FCSTD DOCUMENT  (FreeCAD 0.20R29603 (Git))
Label: samd21pad
License: All rights reserved
LicenseURL: http://en.wikipedia.org/wiki/All_rights_reserved
objects: Sketcher::SketchObject×1
note: 1 computed .brp shape members not serialized (recipe doc carries the construction recipe); baked Part::Feature solids carry a one-line shape summary decoded from their .brp

FEATURE [Sketcher::SketchObject] Sketch  label="Edge Cuts"
  FullyConstrained = false
  sketch-geometry (63):
    g0: ArcOfCircle CenterX=-27.575 CenterY=27.575 CenterZ=0 NormalX=0 NormalY=0 NormalZ=1 AngleXU=0 Radius=1 StartAngle=1.5708 EndAngle=3.14159
    g1: LineSegment StartX=-27.575 StartY=28.575 StartZ=0 EndX=27.575 EndY=28.575 EndZ=0
    g2: ArcOfCircle CenterX=27.575 CenterY=27.575 CenterZ=0 NormalX=0 NormalY=0 NormalZ=1 AngleXU=0 Radius=1 StartAngle=-9e-16 EndAngle=1.5708
    g3: ArcOfCircle CenterX=27.575 CenterY=-27.575 CenterZ=0 NormalX=0 NormalY=0 NormalZ=1 AngleXU=0 Radius=1 StartAngle=4.71239 EndAngle=6.28319
    g4: LineSegment StartX=27.575 StartY=-28.575 StartZ=0 EndX=-27.575 EndY=-28.575 EndZ=0
    g5: ArcOfCircle CenterX=-27.575 CenterY=-27.575 CenterZ=0 NormalX=0 NormalY=0 NormalZ=1 AngleXU=0 Radius=1 StartAngle=3.14159 EndAngle=4.71239
    g6: LineSegment StartX=-28.575 StartY=-27.575 StartZ=0 EndX=-28.575 EndY=27.575 EndZ=0
    g7: GeomPoint X=-28.575 Y=28.575 Z=0
    g8: GeomPoint X=28.575 Y=-28.575 Z=0
    g9: ArcOfCircle CenterX=34.575 CenterY=27.575 CenterZ=0 NormalX=0 NormalY=0 NormalZ=1 AngleXU=0 Radius=1 StartAngle=1.5708 EndAngle=3.14159
    g10: LineSegment StartX=34.575 StartY=28.575 StartZ=0 EndX=89.725 EndY=28.575 EndZ=0
    g11: ArcOfCircle CenterX=89.725 CenterY=27.575 CenterZ=0 NormalX=0 NormalY=0 NormalZ=1 AngleXU=0 Radius=1 StartAngle=-9e-16 EndAngle=1.5708
    g12: LineSegment StartX=90.725 StartY=27.575 StartZ=0 EndX=90.725 EndY=-27.575 EndZ=0
    g13: ArcOfCircle CenterX=89.725 CenterY=-27.575 CenterZ=0 NormalX=0 NormalY=0 NormalZ=1 AngleXU=0 Radius=1 StartAngle=4.71239 EndAngle=6.28319
    g14: ArcOfCircle CenterX=34.575 CenterY=-27.575 CenterZ=0 NormalX=0 NormalY=0 NormalZ=1 AngleXU=0 Radius=1 StartAngle=3.14159 EndAngle=4.71239
    g15: GeomPoint X=37.8345 Y=28.575 Z=0
    g16: GeomPoint X=90.725 Y=-28.575 Z=0
    g17: ArcOfCircle CenterX=34.575 CenterY=-34.575 CenterZ=0 NormalX=0 NormalY=0 NormalZ=1 AngleXU=0 Radius=1 StartAngle=1.5708 EndAngle=3.14159
    g18: ArcOfCircle CenterX=89.725 CenterY=-34.575 CenterZ=0 NormalX=0 NormalY=0 NormalZ=1 AngleXU=0 Radius=1 StartAngle=-9e-16 EndAngle=1.5708
    g19: LineSegment StartX=90.725 StartY=-34.575 StartZ=0 EndX=90.725 EndY=-89.725 EndZ=0
    g20: ArcOfCircle CenterX=89.725 CenterY=-89.725 CenterZ=0 NormalX=0 NormalY=0 NormalZ=1 AngleXU=0 Radius=1 StartAngle=4.71239 EndAngle=6.28319
    g21: LineSegment StartX=89.725 StartY=-90.725 StartZ=0 EndX=34.575 EndY=-90.725 EndZ=0
    g22: ArcOfCircle CenterX=34.575 CenterY=-89.725 CenterZ=0 NormalX=0 NormalY=0 NormalZ=1 AngleXU=0 Radius=1 StartAngle=3.14159 EndAngle=4.71239
    g23: LineSegment StartX=33.575 StartY=-89.725 StartZ=0 EndX=33.575 EndY=-34.575 EndZ=0
    g24: GeomPoint X=33.575 Y=-31.7136 Z=0
    g25: GeomPoint X=90.725 Y=-90.725 Z=0
    g26: LineSegment StartX=29.575 StartY=22.575 StartZ=0 EndX=32.575 EndY=22.575 EndZ=0
    g27: LineSegment StartX=29.575 StartY=18.575 StartZ=0 EndX=32.575 EndY=18.575 EndZ=0
    g28: LineSegment StartX=29.575 StartY=-18.575 StartZ=0 EndX=32.575 EndY=-18.575 EndZ=0
    g29: LineSegment StartX=29.575 StartY=-22.575 StartZ=0 EndX=32.575 EndY=-22.575 EndZ=0
    g30: ArcOfCircle CenterX=29.575 CenterY=23.575 CenterZ=0 NormalX=0 NormalY=0 NormalZ=1 AngleXU=0 Radius=1 StartAngle=3.14159 EndAngle=4.71239
    g31: ArcOfCircle CenterX=32.575 CenterY=23.575 CenterZ=0 NormalX=0 NormalY=0 NormalZ=1 AngleXU=0 Radius=1 StartAngle=4.71239 EndAngle=6.28319
    g32: ArcOfCircle CenterX=32.575 CenterY=17.575 CenterZ=0 NormalX=0 NormalY=0 NormalZ=1 AngleXU=0 Radius=1 StartAngle=-9e-16 EndAngle=1.5708
    g33: ArcOfCircle CenterX=29.575 CenterY=17.575 CenterZ=0 NormalX=0 NormalY=0 NormalZ=1 AngleXU=0 Radius=1 StartAngle=1.5708 EndAngle=3.14159
    g34: LineSegment StartX=28.575 StartY=27.575 StartZ=0 EndX=28.575 EndY=23.575 EndZ=0
    g35: ArcOfCircle CenterX=29.575 CenterY=-17.575 CenterZ=0 NormalX=0 NormalY=0 NormalZ=1 AngleXU=0 Radius=1 StartAngle=3.14159 EndAngle=4.71239
    g36: ArcOfCircle CenterX=32.575 CenterY=-17.575 CenterZ=0 NormalX=0 NormalY=0 NormalZ=1 AngleXU=0 Radius=1 StartAngle=4.71239 EndAngle=6.28319
    g37: ArcOfCircle CenterX=29.575 CenterY=-23.575 CenterZ=0 NormalX=0 NormalY=0 NormalZ=1 AngleXU=0 Radius=1 StartAngle=1.5708 EndAngle=3.14159
    g38: ArcOfCircle CenterX=32.575 CenterY=-23.575 CenterZ=0 NormalX=0 NormalY=0 NormalZ=1 AngleXU=0 Radius=1 StartAngle=1.2e-15 EndAngle=1.5708
    g39: LineSegment StartX=28.575 StartY=17.575 StartZ=0 EndX=28.575 EndY=-17.575 EndZ=0
    g40: LineSegment StartX=28.575 StartY=-23.575 StartZ=0 EndX=28.575 EndY=-27.575 EndZ=0
    g41: LineSegment StartX=33.575 StartY=23.575 StartZ=0 EndX=33.575 EndY=27.575 EndZ=0
    g42: LineSegment StartX=33.575 StartY=17.575 StartZ=0 EndX=33.575 EndY=-17.575 EndZ=0
    g43: LineSegment StartX=33.575 StartY=-23.575 StartZ=0 EndX=33.575 EndY=-27.575 EndZ=0
    g44: LineSegment StartX=39.575 StartY=-29.575 StartZ=0 EndX=39.575 EndY=-32.575 EndZ=0
    g45: LineSegment StartX=43.575 StartY=-29.575 StartZ=0 EndX=43.575 EndY=-32.575 EndZ=0
    g46: LineSegment StartX=80.725 StartY=-29.575 StartZ=0 EndX=80.725 EndY=-32.575 EndZ=0
    g47: LineSegment StartX=84.725 StartY=-29.575 StartZ=0 EndX=84.725 EndY=-32.575 EndZ=0
    g48: ArcOfCircle CenterX=38.575 CenterY=-29.575 CenterZ=0 NormalX=0 NormalY=0 NormalZ=1 AngleXU=0 Radius=1 StartAngle=-9e-16 EndAngle=1.5708
    g49: ArcOfCircle CenterX=38.575 CenterY=-32.575 CenterZ=0 NormalX=0 NormalY=0 NormalZ=1 AngleXU=0 Radius=1 StartAngle=4.71239 EndAngle=6.28319
    g50: ArcOfCircle CenterX=44.575 CenterY=-29.575 CenterZ=0 NormalX=0 NormalY=0 NormalZ=1 AngleXU=0 Radius=1 StartAngle=1.5708 EndAngle=3.14159
    g51: ArcOfCircle CenterX=44.575 CenterY=-32.575 CenterZ=0 NormalX=0 NormalY=0 NormalZ=1 AngleXU=0 Radius=1 StartAngle=3.14159 EndAngle=4.71239
    g52: ArcOfCircle CenterX=79.725 CenterY=-29.575 CenterZ=0 NormalX=0 NormalY=0 NormalZ=1 AngleXU=0 Radius=1 StartAngle=1.5e-15 EndAngle=1.5708
    g53: ArcOfCircle CenterX=79.725 CenterY=-32.575 CenterZ=0 NormalX=0 NormalY=0 NormalZ=1 AngleXU=0 Radius=1 StartAngle=4.71239 EndAngle=6.28319
    g54: ArcOfCircle CenterX=85.725 CenterY=-29.575 CenterZ=0 NormalX=0 NormalY=0 NormalZ=1 AngleXU=0 Radius=1 StartAngle=1.5708 EndAngle=3.14159
    g55: ArcOfCircle CenterX=85.725 CenterY=-32.575 CenterZ=0 NormalX=0 NormalY=0 NormalZ=1 AngleXU=0 Radius=1 StartAngle=3.14159 EndAngle=4.71239
    g56: LineSegment StartX=38.575 StartY=-28.575 StartZ=0 EndX=34.575 EndY=-28.575 EndZ=0
    g57: LineSegment StartX=44.575 StartY=-28.575 StartZ=0 EndX=79.725 EndY=-28.575 EndZ=0
    g58: LineSegment StartX=85.725 StartY=-28.575 StartZ=0 EndX=89.725 EndY=-28.575 EndZ=0
    g59: LineSegment StartX=89.725 StartY=-33.575 StartZ=0 EndX=85.725 EndY=-33.575 EndZ=0
    g60: LineSegment StartX=79.725 StartY=-33.575 StartZ=0 EndX=44.575 EndY=-33.575 EndZ=0
    g61: LineSegment StartX=38.575 StartY=-33.575 StartZ=0 EndX=34.575 EndY=-33.575 EndZ=0
    g62: GeomPoint X=62.15 Y=-28.575 Z=0
  constraints (161):
    c: Tangent(g0,g1) = 1.5708
    c: Tangent(g1,g2) = 1.5708
    c: Tangent(g3,g4) = 1.5708
    c: Tangent(g4,g5) = 1.5708
    c: Tangent(g5,g6) = 1.5708
    c: Tangent(g6,g0) = 1.5708
    c: Horizontal(g1)
    c: Horizontal(g4)
    c: Vertical(g6)
    c: Equal(g2,g3)
    c: Equal(g3,g5)
    c: PointOnObject(g7,g1)
    c: PointOnObject(g7,g6)
    c: PointOnObject(g8,g4)
    c: Radius(g2) = 1
    c: DistanceX(g0,g2) = 57.15
    c: Symmetric(g0,g2,g-2)
    c: Symmetric(g1,g3,g-1)
    c: Tangent(g9,g10) = 1.5708
    c: Tangent(g10,g11) = 1.5708
    c: Tangent(g11,g12) = 1.5708
    c: Tangent(g12,g13) = 1.5708
    c: Horizontal(g10)
    c: Vertical(g12)
    c: Equal(g9,g11)
    c: Equal(g11,g13)
    c: Equal(g13,g14)
    c: PointOnObject(g15,g10)
    c: PointOnObject(g16,g12)
    c: Tangent(g18,g19) = 1.5708
    c: Tangent(g19,g20) = 1.5708
    c: Tangent(g20,g21) = 1.5708
    c: Tangent(g21,g22) = 1.5708
    c: Tangent(g22,g23) = 1.5708
    c: Tangent(g23,g17) = 1.5708
    c: Horizontal(g21)
    c: Vertical(g19)
    c: Vertical(g23)
    c: Equal(g17,g18)
    c: Equal(g18,g20)
    c: Equal(g20,g22)
    c: PointOnObject(g24,g23)
    c: PointOnObject(g25,g19)
    c: PointOnObject(g25,g21)
    c: Equal(g9,g2)
    c: Equal(g10,g1)
    c: Horizontal(g9,g1)
    c: Equal(g17,g2)
    c: Equal(g23,g4)
    c: Vertical(g12,g18)
    c: Horizontal(g27)
    c: Tangent(g30,g26) = -1.5708
    c: Tangent(g33,g27) = 1.5708
    c: Tangent(g32,g27) = 1.5708
    c: Angle(g30) = 1.5708
    c: Radius(g30) = 1
    c: Equal(g31,g30)
    c: Tangent(g26,g31) = -1.5708
    c: Horizontal(g26)
    c: Angle(g33) = 1.5708
    c: Equal(g33,g30)
    c: Angle(g31) = 1.5708
    c: Angle(g32) = 1.5708
    c: Equal(g32,g33)
    c: DistanceY(g27,g26) = 4
    c: Vertical(g26,g27)
    c: Coincident(g34,g30)
    c: Vertical(g34)
    c: Horizontal(g28)
    c: Horizontal(g29)
    c: Tangent(g35,g28) = -1.5708
    c: Tangent(g36,g28) = -1.5708
    c: Angle(g35) = 1.5708
    c: Angle(g36) = 1.5708
    c: Tangent(g37,g29) = 1.5708
    c: Tangent(g38,g29) = 1.5708
    c: Angle(g37) = 1.5708
    c: Angle(g38) = 1.5708
    c: Radius(g35) = 1
    c: Equal(g35,g36)
    c: Equal(g37,g35)
    c: Equal(g38,g35)
    c: Vertical(g29,g28)
    c: DistanceY(g29,g28) = 4
    c: Coincident(g39,g33)
    c: Coincident(g39,g35)
    c: Coincident(g41,g31)
    c: Vertical(g41)
    c: Equal(g27,g26)
    c: Coincident(g42,g32)
    c: Coincident(g42,g36)
    c: Vertical(g42)
    c: Equal(g29,g28)
    c: Coincident(g43,g38)
    c: Vertical(g43)
    c: Tangent(g41,g9) = 1.5708
    c: Tangent(g43,g14) = -1.5708
    c: Equal(g6,g1)
    c: Tangent(g34,g2) = 1.5708
    c: Tangent(g40,g3) = 1.5708
    c: Symmetric(g27,g28,g-1)
    c: DistanceX(g2,g9) = 5
    c: DistanceY(g26,g1) = 6
    c: Equal(g12,g10)
    c: Vertical(g44)
    c: Vertical(g45)
    c: Vertical(g46)
    c: Vertical(g47)
    c: Tangent(g48,g44) = 1.5708
    c: Tangent(g49,g44) = 1.5708
    c: Tangent(g50,g45) = -1.5708
    c: Tangent(g51,g45) = -1.5708
    c: Tangent(g53,g46) = 1.5708
    c: Tangent(g52,g46) = 1.5708
    c: Tangent(g54,g47) = -1.5708
    c: Tangent(g55,g47) = -1.5708
    c: Angle(g49) = 1.5708
    c: Angle(g48) = 1.5708
    c: Angle(g50) = 1.5708
    c: Angle(g51) = 1.5708
    c: Angle(g52) = 1.5708
    c: Angle(g53) = 1.5708
    c: Angle(g54) = 1.5708
    c: Angle(g55) = 1.5708
    c: Equal(g48,g30)
    c: Equal(g49,g48)
    c: Equal(g50,g48)
    c: Equal(g51,g48)
    c: Equal(g52,g48)
    c: Equal(g53,g52)
    c: Equal(g55,g52)
    c: Equal(g54,g52)
    c: Equal(g45,g44)
    c: Equal(g46,g47)
    c: Horizontal(g45,g44)
    c: Horizontal(g46,g47)
    c: Coincident(g56,g48)
    c: Coincident(g57,g50)
    c: Coincident(g57,g52)
    c: Horizontal(g57)
    c: Coincident(g58,g54)
    c: Coincident(g59,g55)
    c: Coincident(g60,g53)
    c: Coincident(g60,g51)
    c: Coincident(g61,g49)
    c: Horizontal(g56)
    c: Horizontal(g59)
    c: Horizontal(g60)
    c: Horizontal(g61)
    c: Symmetric(g13,g14,g62)
    c: DistanceX(g44,g45) = 4
    c: DistanceX(g46,g47) = 4
    c: Symmetric(g52,g50,g62)
    c: Tangent(g58,g13) = -1.5708
    c: Tangent(g56,g14) = 1.5708
    c: Tangent(g61,g17) = -1.5708
    c: Tangent(g59,g18) = -1.5708
    c: DistanceY(g18,g13) = 5
    c: DistanceX(g47,g12) = 6
    c: Equal(g21,g19)
    c: Tangent(g40,g37) = -1.5708
